# Revit family: Drain_Cornice_6_Inch_Top-Zurn-Z185
name_source: partatom
category: Plumbing Fixtures
units: mm (PartAtom-declared; Revit-internal decimal feet)

## family parameters
Always vertical = Yes
Cut with Voids When Loaded = No
Maintain Annotation Orientation = No
OmniClass Number = 23.70.50.21.24.14
OmniClass Title = Deck Waste Water Drains
Part Type = Normal
Room Calculation Point = No
Round Connector Dimension = Use Radius
Shared = No
Work Plane-Based = No

## types (4) — shared parameters
Assembly Code = D2040200
CW Connection = No
Default Elevation = 30 "
Description = 6 [152] DIAMETER CORNICE DRAIN W/ 90° OUTLET
Dome Open Area = 11.000 in²
HW Connection = No
Main Material = Iron - Zurn - Cast - Painted - Blue
Manufacturer = Zurn Water, LLC
Manufacurer Brand = Zurn
Modified Date = 01/05/2025
Product Documentation Link = https://files.zurn.com
Product Installation Sheet URL = https://files.zurn.com
Product Page URL = https://www.zurn.com
Product data url = https://www.bimobject.com
URL = www.zurn.com
Vent Connection = No
WFU = 1
Waste Connection = Yes
zero-valued in all types: CWFU, HWFU

## per-type parameters (varying)
| type | Approx. Wt. Lbs. | Body Height (E) | Dome Material | Model | Pipe Size 'A' (Inner Diameter) | Pipe Size 'A' (Inner Radius) | Pipe Size 'A' (Nominal Diameter) | Pipe Size 'A' (Nominal Radius) | Pipe Size 'A' (Outer Diameter) | Pipe Size 'A' (Outer Radius) |
| ZRB185-3 Inch Threaded Outlet | 8.00 lb | 5.125 " | Bronze - Zurn - Polished | ZRB185 | 3.068 " | 1.534 " | 3 " | 1.5 " | 3.5 " | 1.75 " |
| ZRB185-4 Inch Threaded Outlet | 10.00 lb | 5.625 " | Bronze - Zurn - Polished | ZRB185 | 4.026 " | 2.013 " | 4 " | 2 " | 4.5 " | 2.25 " |
| ZN185-4 Inch Threaded Outlet | 10.00 lb | 5.625 " | Bronze - Zurn - Polished Nickel | ZN185 | 4.026 " | 2.013 " | 4 " | 2 " | 4.5 " | 2.25 " |
| ZN185-3 Inch Threaded Outlet | 8.00 lb | 5.125 " | Bronze - Zurn - Polished Nickel | ZN185 | 3.068 " | 1.534 " | 3 " | 1.5 " | 3.5 " | 1.75 " |

## geometry (parser evidence)
native form markers: Sweep x8
no freeform markers — native parametric forms only
